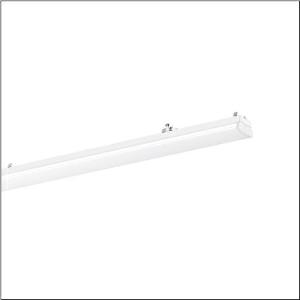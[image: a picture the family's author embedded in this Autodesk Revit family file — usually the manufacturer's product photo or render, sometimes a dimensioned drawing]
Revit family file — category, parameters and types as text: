
# Revit family: licross_21_recessed_opal_mo_52tl1dmn46xg
name_source: partatom
category: Lighting Fixtures
units: mm (PartAtom-declared; Revit-internal decimal feet)

## family parameters
Cut with Voids When Loaded = No
Host = Face
Light Source = No
Part Type = Normal
Room Calculation Point = No
Round Connector Dimension = Use Diameter
Shared = No

## types (1)
- --- (1 x LED, 6270 lm, 35 W, 4000K)
    Apparent Load = 35 VA
    CIE Flux Codes = 44 73 91 87 100
    Color Rendering = 80
    Color Temperature = 4000K
    Default Elevation = 1800 mm
    Description = Licross 21 recessed opal MO, luminaire insert, of sheet steel, galvanised, coil coated, white, length: 1.500mm, width: 66mm, height: 67mm, LED rated luminous flux: 6.270lm, light colour: 840, SDCM (Standard Deviation of Colour Matching)MacAdam ≤ 3 SDCM (initial), control gear: ON/OFF Multilumen, with plug, 3-pole, with phase selection, mains connection: 220..240V, AC, 50/60Hz, rated input power: 35W, internal wiring halogen-free, primary optical cover: cover, of PMMA, light emission: direct with ceiling illumination distribution, primary light characteristic: symmetric, protection rating (complete): IP40, insulation class (complete): insulation class I (protective earthing), certification: CE, ENEC, VDE, UKCA, protection symbol: D if used in an environment without relevant dust loads with corresponding accessories, impact resistance: IK06, permissible ambient temperature for indoor applications: -35..+50°C, corresponds to IFS (International Featured Standards) requirements for safety and quality in the food industry, reducing of maximum allowable ambient temperature of 5°C with ceiling mounting, LABS conformity tested according to VDMA 24364:2018-05, The light source and the operating device comply with the requirements of the Ecodesign Regulation (EU) 2019/2020 and are replaceable in accordance with this regulation, packaging unit: 1 piece
    Height = 83 mm
    Lamp = 1 x LED
    Lamp Light Flux = 6270 lm
    Lamp Power = 35 W
    Lamp count = 1
    Length = 1500 mm
    Luminous efficacy = 179 lm/W
    Manufacturer = Siteco
    ModVariant = No
    Model = 52TL1DMN46XG
    Mounting Place = Ceiling
    Mounting Type = Pendant
    Number of Poles = 1
    OnlyDefault = Yes
    Power Factor = 1
    Product Name = Licross 21 recessed opal MO
    Product group = luminaire insert | ceiling pendant
    ProductGroupID = 901
    Protection Class = Protection class I
    Protection Degree = IP 40
    RLX_Detail_Level = 1
    RLX_Emergency_Light_Flux = 0 lm
    RLX_Emergency_Type = 0
    RLX_Emergency_Type_DB = No
    RlxData = <blob elided: 25129 chars, md5=c91f15de>
    Socket = socket
    Standby Power = 0 W
    System Light Flux = 6270 lm
    System Power = 35 W
    Type Comments = factory setting: luminous flux: 100 % | (A | C | E) | 81 mA
    Type Image = l_1313666.jpg
    URL = http://relux.com
    VarID = @adj_045953
    Voltage = 0 V
    Weight = 0.00 kg
    Width = 76 mm

## geometry (parser evidence)
native form markers: Blend x4, Sweep x12
no freeform markers — native parametric forms only
